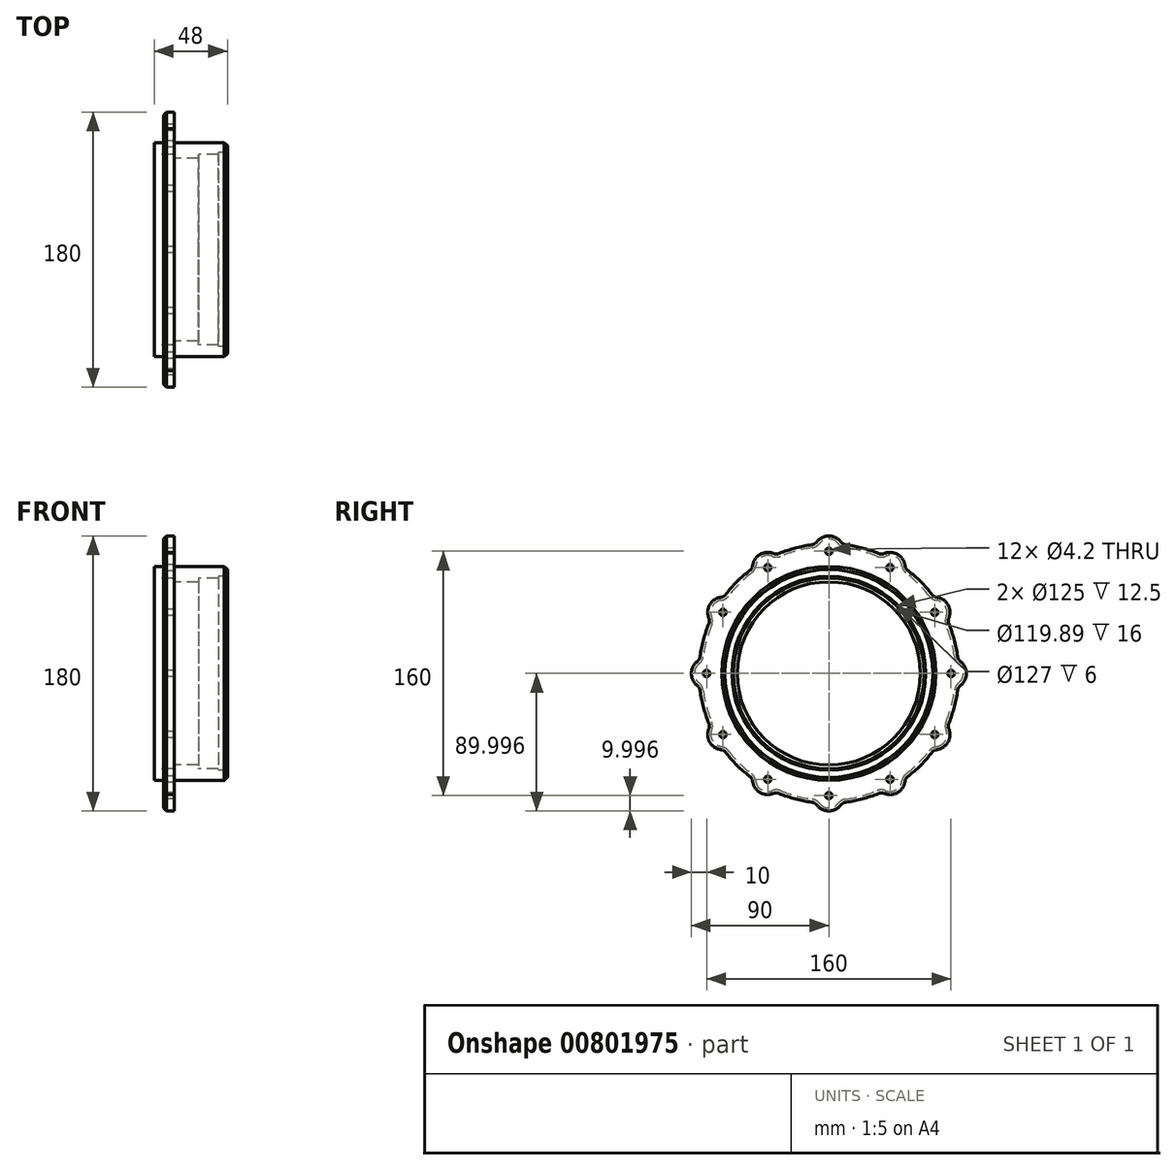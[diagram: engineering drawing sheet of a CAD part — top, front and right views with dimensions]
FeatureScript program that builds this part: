
annotation { "Feature Type Name" : "Feature", "Feature Type Description" : "" }
export const myFeature = defineFeature(function(context is Context, id is Id, definition is map)
    precondition{}
    {
        {
            var Q0;
            Q0=qCreatedBy(makeId("Front.planeOp"),FACE);
            var sketch = newSketch(context, id + "F0", { "sketchPlane" : qUnion([Q0])});
            skLineSegment(sketch, "E0", {"start": v(-16.87, 26.2) * mm, "end": v(-9.87, 26.2) * mm});
            skLineSegment(sketch, "E1", {"start": v(-9.87, 26.2) * mm, "end": v(-9.87, 6.2) * mm});
            skLineSegment(sketch, "E2", {"start": v(-16.87, 26.2) * mm, "end": v(-16.87, 6.2) * mm});
            skLineSegment(sketch, "E3", {"start": v(-16.87, 6.2) * mm, "end": v(-22.87, 6.2) * mm});
            skLineSegment(sketch, "E4", {"start": v(-22.87, 6.2) * mm, "end": v(-22.87, -1.3) * mm});
            skLineSegment(sketch, "E5", {"start": v(-22.87, -1.3) * mm, "end": v(-9.87, -1.3) * mm});
            skLineSegment(sketch, "E6", {"start": v(-9.87, -1.3) * mm, "end": v(-9.87, -3.85) * mm});
            skLineSegment(sketch, "E7", {"start": v(-9.87, -3.85) * mm, "end": v(6.13, -3.85) * mm});
            skLineSegment(sketch, "E8", {"start": v(6.13, -3.85) * mm, "end": v(6.13, -1.3) * mm});
            skLineSegment(sketch, "E9", {"start": v(6.13, -1.3) * mm, "end": v(19.13, -1.3) * mm});
            skLineSegment(sketch, "E10", {"start": v(-16.87, -63.8) * mm, "end": v(53.32, -63.8) * mm, "construction": true});
            skLineSegment(sketch, "E11", {"start": v(19.13, -1.3) * mm, "end": v(19.13, -0.3) * mm});
            skLineSegment(sketch, "E12", {"start": v(19.13, -0.3) * mm, "end": v(25.13, -0.3) * mm});
            skLineSegment(sketch, "E13", {"start": v(-9.87, 6.2) * mm, "end": v(25.13, 6.2) * mm});
            skLineSegment(sketch, "E14", {"start": v(25.13, 6.2) * mm, "end": v(25.13, -0.3) * mm});
            skSolve(sketch);
        }
        {
            var Q0;
            Q0=qSketchRegion(id+"F0",true);
            var Q1;
            Q1=sQuery(id+"F0.wireOp",EDGE,"E10");
            revolve(context, id + "F1", {"entities" : qUnion([Q0]), "axis" : qUnion([Q1]), "revolveType" : RevolveType.FULL});
        }
        {
            var Q0;
            Q0=makeQuery(id+"F1.opRevolve","SWEPT_FACE",FACE,{"disambiguationData":[OSD([sQuery(id+"F0.wireOp",EDGE,"E2")])]});
            var sketch = newSketch(context, id + "F2", { "sketchPlane" : qUnion([Q0])});
            skLineSegment(sketch, "E15", {"start": v(0, -63.8) * mm, "end": v(0, 16.2) * mm, "construction": true});
            skPoint(sketch, "E16", {"position": v(0, 16.2) * mm});
            skPoint(sketch, "E17.1.0", {"position": v(-40, 5.49) * mm});
            skPoint(sketch, "E17.2.0", {"position": v(-69.28, -23.8) * mm});
            skPoint(sketch, "E17.3.0", {"position": v(-80, -63.8) * mm});
            skPoint(sketch, "E17.4.0", {"position": v(-69.28, -103.8) * mm});
            skPoint(sketch, "E17.5.0", {"position": v(-40, -133.08) * mm});
            skPoint(sketch, "E17.6.0", {"position": v(0, -143.8) * mm});
            skPoint(sketch, "E17.7.0", {"position": v(40, -133.08) * mm});
            skPoint(sketch, "E17.8.0", {"position": v(69.28, -103.8) * mm});
            skPoint(sketch, "E17.9.0", {"position": v(80, -63.8) * mm});
            skPoint(sketch, "E17.10.0", {"position": v(69.28, -23.8) * mm});
            skPoint(sketch, "E17.11.0", {"position": v(40, 5.49) * mm});
            skPoint(sketch, "E17.center", {"position": v(0, -63.8) * mm});
            skSolve(sketch);
        }
        {
            var Q0;
            Q0=sQuery(id+"F2.wireOp",VERTEX,"E16");
            var Q1;
            Q1=sQuery(id+"F2.wireOp",VERTEX,"E17.11.0");
            var Q2;
            Q2=sQuery(id+"F2.wireOp",VERTEX,"E17.10.0");
            var Q3;
            Q3=sQuery(id+"F2.wireOp",VERTEX,"E17.9.0");
            var Q4;
            Q4=sQuery(id+"F2.wireOp",VERTEX,"E17.8.0");
            var Q5;
            Q5=sQuery(id+"F2.wireOp",VERTEX,"E17.7.0");
            var Q6;
            Q6=sQuery(id+"F2.wireOp",VERTEX,"E17.6.0");
            var Q7;
            Q7=sQuery(id+"F2.wireOp",VERTEX,"E17.5.0");
            var Q8;
            Q8=sQuery(id+"F2.wireOp",VERTEX,"E17.4.0");
            var Q9;
            Q9=sQuery(id+"F2.wireOp",VERTEX,"E17.3.0");
            var Q10;
            Q10=sQuery(id+"F2.wireOp",VERTEX,"E17.2.0");
            var Q11;
            Q11=sQuery(id+"F2.wireOp",VERTEX,"E17.1.0");
            var Q12;
            Q12=makeQuery(id+"F1.opRevolve","SWEPT_BODY",BODY,{"disambiguationData":[OSD([sQuery(id+"F0.wireOp",EDGE,"E0"),sQuery(id+"F0.wireOp",EDGE,"E1"),sQuery(id+"F0.wireOp",EDGE,"E2"),sQuery(id+"F0.wireOp",EDGE,"E3"),sQuery(id+"F0.wireOp",EDGE,"E4"),sQuery(id+"F0.wireOp",EDGE,"E5"),sQuery(id+"F0.wireOp",EDGE,"E6"),sQuery(id+"F0.wireOp",EDGE,"E7"),sQuery(id+"F0.wireOp",EDGE,"E8"),sQuery(id+"F0.wireOp",EDGE,"E9"),sQuery(id+"F0.wireOp",EDGE,"E11"),sQuery(id+"F0.wireOp",EDGE,"E12"),sQuery(id+"F0.wireOp",EDGE,"E13"),sQuery(id+"F0.wireOp",EDGE,"E14")])]});
            hole(context, id + "F3", {"style" : HoleStyle.SIMPLE, "endStyle" : HoleEndStyle.THROUGH, "standardTappedOrClearance" : lookupTablePath({ "standard" : "ISO", "engagement" : "75%", "pitch" : "0.8 mm", "size" : "M5", "type" : "Tapped" }), "standardBlindInLast" : lookupTablePath({ "standard" : "ISO", "engagement" : "75%", "pitch" : "0.8 mm", "size" : "M5", "type" : "Tapped" }), "holeDiameter" : 4.2 * mm, "showTappedDepth" : true, "isTappedThrough" : true, "tappedDepth" : 16.82 * mm, "tapClearance" : 3, "startFromSketch" : true, "locations" : qUnion([Q0, Q1, Q2, Q3, Q4, Q5, Q6, Q7, Q8, Q9, Q10, Q11]), "scope" : qUnion([Q12]), "majorDiameter" : 5 * mm});
        }
        {
            var Q0;
            Q0=makeQuery(id+"F1.opRevolve","SWEPT_FACE",FACE,{"disambiguationData":[OSD([sQuery(id+"F0.wireOp",EDGE,"E1")])]});
            var sketch = newSketch(context, id + "F4", { "sketchPlane" : qUnion([Q0])});
            skArc(sketch, "E18", {"start": v(45, 14.15) * mm, "mid": v(40.7, 15.46) * mm, "end": v(36.24, 14.75) * mm});
            skArc(sketch, "E19", {"start": v(7.89, 22.35) * mm, "mid": v(4.39, 25.2) * mm, "end": v(0, 26.2) * mm});
            skArc(sketch, "E20", {"start": v(32.45, 14.77) * mm, "mid": v(22, 18.3) * mm, "end": v(11.18, 20.47) * mm});
            skLineSegment(sketch, "E21", {"start": v(0, -63.8) * mm, "end": v(0, 34.34) * mm, "construction": true});
            skLineSegment(sketch, "E22", {"start": v(0, -63.8) * mm, "end": v(49.04, 21.14) * mm, "construction": true});
            skPoint(sketch, "E23.visualSharp", {"position": v(8.91, 20.74) * mm});
            skArc(sketch, "E23.filletArc", {"start": v(7.89, 22.35) * mm, "mid": v(9.35, 21.09) * mm, "end": v(11.18, 20.47) * mm});
            skPoint(sketch, "E24.visualSharp", {"position": v(34.55, 13.87) * mm});
            skArc(sketch, "E24.filletArc", {"start": v(32.45, 14.77) * mm, "mid": v(34.35, 14.39) * mm, "end": v(36.24, 14.75) * mm});
            skPoint(sketch, "E25.1.0", {"position": v(-34.55, 13.87) * mm});
            skArc(sketch, "E25.1.1", {"start": v(-11.18, 20.47) * mm, "mid": v(-22, 18.3) * mm, "end": v(-32.45, 14.77) * mm});
            skArc(sketch, "E25.1.2", {"start": v(-36.24, 14.75) * mm, "mid": v(-40.7, 15.46) * mm, "end": v(-45, 14.15) * mm});
            skPoint(sketch, "E25.1.3", {"position": v(-8.91, 20.74) * mm});
            skArc(sketch, "E25.1.4", {"start": v(0, 26.2) * mm, "mid": v(-4.39, 25.2) * mm, "end": v(-7.89, 22.35) * mm});
            skArc(sketch, "E25.1.5", {"start": v(-11.18, 20.47) * mm, "mid": v(-9.35, 21.09) * mm, "end": v(-7.89, 22.35) * mm});
            skArc(sketch, "E25.1.6", {"start": v(-36.24, 14.75) * mm, "mid": v(-34.35, 14.39) * mm, "end": v(-32.45, 14.77) * mm});
            skPoint(sketch, "E25.2.0", {"position": v(-68.75, -13.8) * mm});
            skArc(sketch, "E25.2.1", {"start": v(-51.8, 3.6) * mm, "mid": v(-60.1, -3.7) * mm, "end": v(-67.39, -11.98) * mm});
            skArc(sketch, "E25.2.2", {"start": v(-70.66, -13.89) * mm, "mid": v(-74.87, -15.5) * mm, "end": v(-77.94, -18.8) * mm});
            skPoint(sketch, "E25.2.3", {"position": v(-49.99, 4.95) * mm});
            skArc(sketch, "E25.2.4", {"start": v(-45, 14.15) * mm, "mid": v(-48.3, 11.07) * mm, "end": v(-49.9, 6.87) * mm});
            skArc(sketch, "E25.2.5", {"start": v(-51.8, 3.6) * mm, "mid": v(-50.53, 5.04) * mm, "end": v(-49.9, 6.87) * mm});
            skArc(sketch, "E25.2.6", {"start": v(-70.66, -13.89) * mm, "mid": v(-68.84, -13.26) * mm, "end": v(-67.39, -11.98) * mm});
            skPoint(sketch, "E25.3.0", {"position": v(-84.53, -54.88) * mm});
            skArc(sketch, "E25.3.1", {"start": v(-78.56, -31.34) * mm, "mid": v(-82.1, -41.8) * mm, "end": v(-84.26, -52.62) * mm});
            skArc(sketch, "E25.3.2", {"start": v(-86.15, -55.9) * mm, "mid": v(-88.98, -59.4) * mm, "end": v(-90, -63.8) * mm});
            skPoint(sketch, "E25.3.3", {"position": v(-77.66, -29.25) * mm});
            skArc(sketch, "E25.3.4", {"start": v(-77.94, -18.8) * mm, "mid": v(-79.26, -23.1) * mm, "end": v(-78.55, -27.55) * mm});
            skArc(sketch, "E25.3.5", {"start": v(-78.56, -31.34) * mm, "mid": v(-78.18, -29.45) * mm, "end": v(-78.55, -27.55) * mm});
            skArc(sketch, "E25.3.6", {"start": v(-86.15, -55.9) * mm, "mid": v(-84.88, -54.45) * mm, "end": v(-84.26, -52.62) * mm});
            skPoint(sketch, "E25.4.0", {"position": v(-77.66, -98.34) * mm});
            skArc(sketch, "E25.4.1", {"start": v(-84.26, -74.97) * mm, "mid": v(-82.1, -85.8) * mm, "end": v(-78.56, -96.25) * mm});
            skArc(sketch, "E25.4.2", {"start": v(-78.55, -100.04) * mm, "mid": v(-79.26, -104.48) * mm, "end": v(-77.94, -108.8) * mm});
            skPoint(sketch, "E25.4.3", {"position": v(-84.53, -72.7) * mm});
            skArc(sketch, "E25.4.4", {"start": v(-90, -63.8) * mm, "mid": v(-88.98, -68.18) * mm, "end": v(-86.15, -71.68) * mm});
            skArc(sketch, "E25.4.5", {"start": v(-84.26, -74.97) * mm, "mid": v(-84.88, -73.14) * mm, "end": v(-86.15, -71.68) * mm});
            skArc(sketch, "E25.4.6", {"start": v(-78.55, -100.04) * mm, "mid": v(-78.18, -98.14) * mm, "end": v(-78.56, -96.25) * mm});
            skPoint(sketch, "E25.5.0", {"position": v(-49.99, -132.54) * mm});
            skArc(sketch, "E25.5.1", {"start": v(-67.39, -115.6) * mm, "mid": v(-60.1, -123.9) * mm, "end": v(-51.8, -131.18) * mm});
            skArc(sketch, "E25.5.2", {"start": v(-49.9, -134.45) * mm, "mid": v(-48.3, -138.66) * mm, "end": v(-45, -141.74) * mm});
            skPoint(sketch, "E25.5.3", {"position": v(-68.75, -113.78) * mm});
            skArc(sketch, "E25.5.4", {"start": v(-77.94, -108.8) * mm, "mid": v(-74.87, -112.09) * mm, "end": v(-70.66, -113.7) * mm});
            skArc(sketch, "E25.5.5", {"start": v(-67.39, -115.6) * mm, "mid": v(-68.84, -114.33) * mm, "end": v(-70.66, -113.7) * mm});
            skArc(sketch, "E25.5.6", {"start": v(-49.9, -134.45) * mm, "mid": v(-50.53, -132.63) * mm, "end": v(-51.8, -131.18) * mm});
            skPoint(sketch, "E25.6.0", {"position": v(-8.91, -148.33) * mm});
            skArc(sketch, "E25.6.1", {"start": v(-32.45, -142.36) * mm, "mid": v(-22, -145.9) * mm, "end": v(-11.18, -148.06) * mm});
            skArc(sketch, "E25.6.2", {"start": v(-7.89, -149.94) * mm, "mid": v(-4.39, -152.78) * mm, "end": v(0, -153.8) * mm});
            skPoint(sketch, "E25.6.3", {"position": v(-34.55, -141.46) * mm});
            skArc(sketch, "E25.6.4", {"start": v(-45, -141.74) * mm, "mid": v(-40.7, -143.05) * mm, "end": v(-36.24, -142.34) * mm});
            skArc(sketch, "E25.6.5", {"start": v(-32.45, -142.36) * mm, "mid": v(-34.35, -141.98) * mm, "end": v(-36.24, -142.34) * mm});
            skArc(sketch, "E25.6.6", {"start": v(-7.89, -149.94) * mm, "mid": v(-9.35, -148.67) * mm, "end": v(-11.18, -148.06) * mm});
            skPoint(sketch, "E25.7.0", {"position": v(34.55, -141.46) * mm});
            skArc(sketch, "E25.7.1", {"start": v(11.18, -148.06) * mm, "mid": v(22, -145.9) * mm, "end": v(32.45, -142.36) * mm});
            skArc(sketch, "E25.7.2", {"start": v(36.24, -142.34) * mm, "mid": v(40.7, -143.05) * mm, "end": v(45, -141.74) * mm});
            skPoint(sketch, "E25.7.3", {"position": v(8.91, -148.33) * mm});
            skArc(sketch, "E25.7.4", {"start": v(0, -153.8) * mm, "mid": v(4.39, -152.78) * mm, "end": v(7.89, -149.94) * mm});
            skArc(sketch, "E25.7.5", {"start": v(11.18, -148.06) * mm, "mid": v(9.35, -148.67) * mm, "end": v(7.89, -149.94) * mm});
            skArc(sketch, "E25.7.6", {"start": v(36.24, -142.34) * mm, "mid": v(34.35, -141.98) * mm, "end": v(32.45, -142.36) * mm});
            skPoint(sketch, "E25.8.0", {"position": v(68.75, -113.78) * mm});
            skArc(sketch, "E25.8.1", {"start": v(51.8, -131.18) * mm, "mid": v(60.1, -123.9) * mm, "end": v(67.39, -115.6) * mm});
            skArc(sketch, "E25.8.2", {"start": v(70.66, -113.7) * mm, "mid": v(74.87, -112.09) * mm, "end": v(77.94, -108.8) * mm});
            skPoint(sketch, "E25.8.3", {"position": v(49.99, -132.54) * mm});
            skArc(sketch, "E25.8.4", {"start": v(45, -141.74) * mm, "mid": v(48.3, -138.66) * mm, "end": v(49.9, -134.45) * mm});
            skArc(sketch, "E25.8.5", {"start": v(51.8, -131.18) * mm, "mid": v(50.53, -132.63) * mm, "end": v(49.9, -134.45) * mm});
            skArc(sketch, "E25.8.6", {"start": v(70.66, -113.7) * mm, "mid": v(68.84, -114.33) * mm, "end": v(67.39, -115.6) * mm});
            skPoint(sketch, "E25.9.0", {"position": v(84.53, -72.7) * mm});
            skArc(sketch, "E25.9.1", {"start": v(78.56, -96.25) * mm, "mid": v(82.1, -85.8) * mm, "end": v(84.26, -74.97) * mm});
            skArc(sketch, "E25.9.2", {"start": v(86.15, -71.68) * mm, "mid": v(88.98, -68.18) * mm, "end": v(90, -63.8) * mm});
            skPoint(sketch, "E25.9.3", {"position": v(77.66, -98.34) * mm});
            skArc(sketch, "E25.9.4", {"start": v(77.94, -108.8) * mm, "mid": v(79.26, -104.48) * mm, "end": v(78.55, -100.04) * mm});
            skArc(sketch, "E25.9.5", {"start": v(78.56, -96.25) * mm, "mid": v(78.18, -98.14) * mm, "end": v(78.55, -100.04) * mm});
            skArc(sketch, "E25.9.6", {"start": v(86.15, -71.68) * mm, "mid": v(84.88, -73.14) * mm, "end": v(84.26, -74.97) * mm});
            skPoint(sketch, "E25.10.0", {"position": v(77.66, -29.25) * mm});
            skArc(sketch, "E25.10.1", {"start": v(84.26, -52.62) * mm, "mid": v(82.1, -41.8) * mm, "end": v(78.56, -31.34) * mm});
            skArc(sketch, "E25.10.2", {"start": v(78.55, -27.55) * mm, "mid": v(79.26, -23.1) * mm, "end": v(77.94, -18.8) * mm});
            skPoint(sketch, "E25.10.3", {"position": v(84.53, -54.88) * mm});
            skArc(sketch, "E25.10.4", {"start": v(90, -63.8) * mm, "mid": v(88.98, -59.4) * mm, "end": v(86.15, -55.9) * mm});
            skArc(sketch, "E25.10.5", {"start": v(84.26, -52.62) * mm, "mid": v(84.88, -54.45) * mm, "end": v(86.15, -55.9) * mm});
            skArc(sketch, "E25.10.6", {"start": v(78.55, -27.55) * mm, "mid": v(78.18, -29.45) * mm, "end": v(78.56, -31.34) * mm});
            skPoint(sketch, "E25.11.0", {"position": v(49.99, 4.95) * mm});
            skArc(sketch, "E25.11.1", {"start": v(67.39, -11.98) * mm, "mid": v(60.1, -3.7) * mm, "end": v(51.8, 3.6) * mm});
            skArc(sketch, "E25.11.2", {"start": v(49.9, 6.87) * mm, "mid": v(48.3, 11.07) * mm, "end": v(45, 14.15) * mm});
            skPoint(sketch, "E25.11.3", {"position": v(68.75, -13.8) * mm});
            skArc(sketch, "E25.11.4", {"start": v(77.94, -18.8) * mm, "mid": v(74.87, -15.5) * mm, "end": v(70.66, -13.89) * mm});
            skArc(sketch, "E25.11.5", {"start": v(67.39, -11.98) * mm, "mid": v(68.84, -13.26) * mm, "end": v(70.66, -13.89) * mm});
            skArc(sketch, "E25.11.6", {"start": v(49.9, 6.87) * mm, "mid": v(50.53, 5.04) * mm, "end": v(51.8, 3.6) * mm});
            skCircle(sketch, "E26", {"center": v(0, -63.8) * mm, "radius": 105.65 * mm});
            skSolve(sketch);
        }
        {
            var Q0;
            Q0=qSketchRegion(id+"F4",true);
            extrude(context, id + "F5", {"entities" : qUnion([Q0]), "operationType" : NewBodyOperationType.REMOVE, "endBound" : BoundingType.THROUGH_ALL, "oppositeDirection" : true, "depth" : 25 * mm, "offsetDistance" : 25 * mm});
        }
        {
            var Q0;
            Q0=makeQuery(id+"F1.opRevolve","SWEPT_EDGE",EDGE,{"disambiguationData":[OSD([sQuery(id+"F0.wireOp",EDGE,"E13"),sQuery(id+"F0.wireOp",EDGE,"E14")])]});
            var Q1;
            Q1=makeQuery(id+"F1.opRevolve","SWEPT_EDGE",EDGE,{"disambiguationData":[OSD([sQuery(id+"F0.wireOp",EDGE,"E0"),sQuery(id+"F0.wireOp",EDGE,"E2")])]});
            chamfer(context, id + "F6", {"entities" : qUnion([Q0, Q1]), "width" : 2 * mm, "tangentPropagation" : true});
        }
        {
            var Q0;
            Q0=makeQuery(id+"F5.boolean.opBoolean","INTERSECT",EDGE,{"derivedFrom":[makeQuery(id+"F1.opRevolve","SWEPT_FACE",FACE,{"disambiguationData":[OSD([sQuery(id+"F0.wireOp",EDGE,"E2")])]}),makeQuery(id+"F5.opExtrude","SWEPT_FACE",FACE,{"disambiguationData":[OSD([sQuery(id+"F4.wireOp",EDGE,"E20")])]})]});
            chamfer(context, id + "F7", {"entities" : qUnion([Q0]), "width" : 2 * mm, "tangentPropagation" : true});
        }
        {
            var Q0;
            Q0=makeQuery(id+"F1.opRevolve","SWEPT_EDGE",EDGE,{"disambiguationData":[OSD([sQuery(id+"F0.wireOp",EDGE,"E8"),sQuery(id+"F0.wireOp",EDGE,"E9")])]});
            fillet(context, id + "F8", {"entities" : qUnion([Q0]), "radius" : .5 * mm, "tangentPropagation" : true, "allowEdgeOverflow" : false});
        }
        {
            var Q0;
            Q0=makeQuery(id+"F1.opRevolve","SWEPT_EDGE",EDGE,{"disambiguationData":[OSD([sQuery(id+"F0.wireOp",EDGE,"E5"),sQuery(id+"F0.wireOp",EDGE,"E6")])]});
            fillet(context, id + "F9", {"entities" : qUnion([Q0]), "radius" : .5 * mm, "tangentPropagation" : true, "allowEdgeOverflow" : false});
        }
        {
            var Q0;
            Q0=makeQuery(id+"F1.opRevolve","SWEPT_EDGE",EDGE,{"disambiguationData":[OSD([sQuery(id+"F0.wireOp",EDGE,"E2"),sQuery(id+"F0.wireOp",EDGE,"E3")])]});
            var Q1;
            Q1=makeQuery(id+"F1.opRevolve","SWEPT_EDGE",EDGE,{"disambiguationData":[OSD([sQuery(id+"F0.wireOp",EDGE,"E1"),sQuery(id+"F0.wireOp",EDGE,"E13")])]});
            fillet(context, id + "F10", {"entities" : qUnion([Q0, Q1]), "radius" : .5 * mm, "tangentPropagation" : true, "allowEdgeOverflow" : false});
        }
    });
